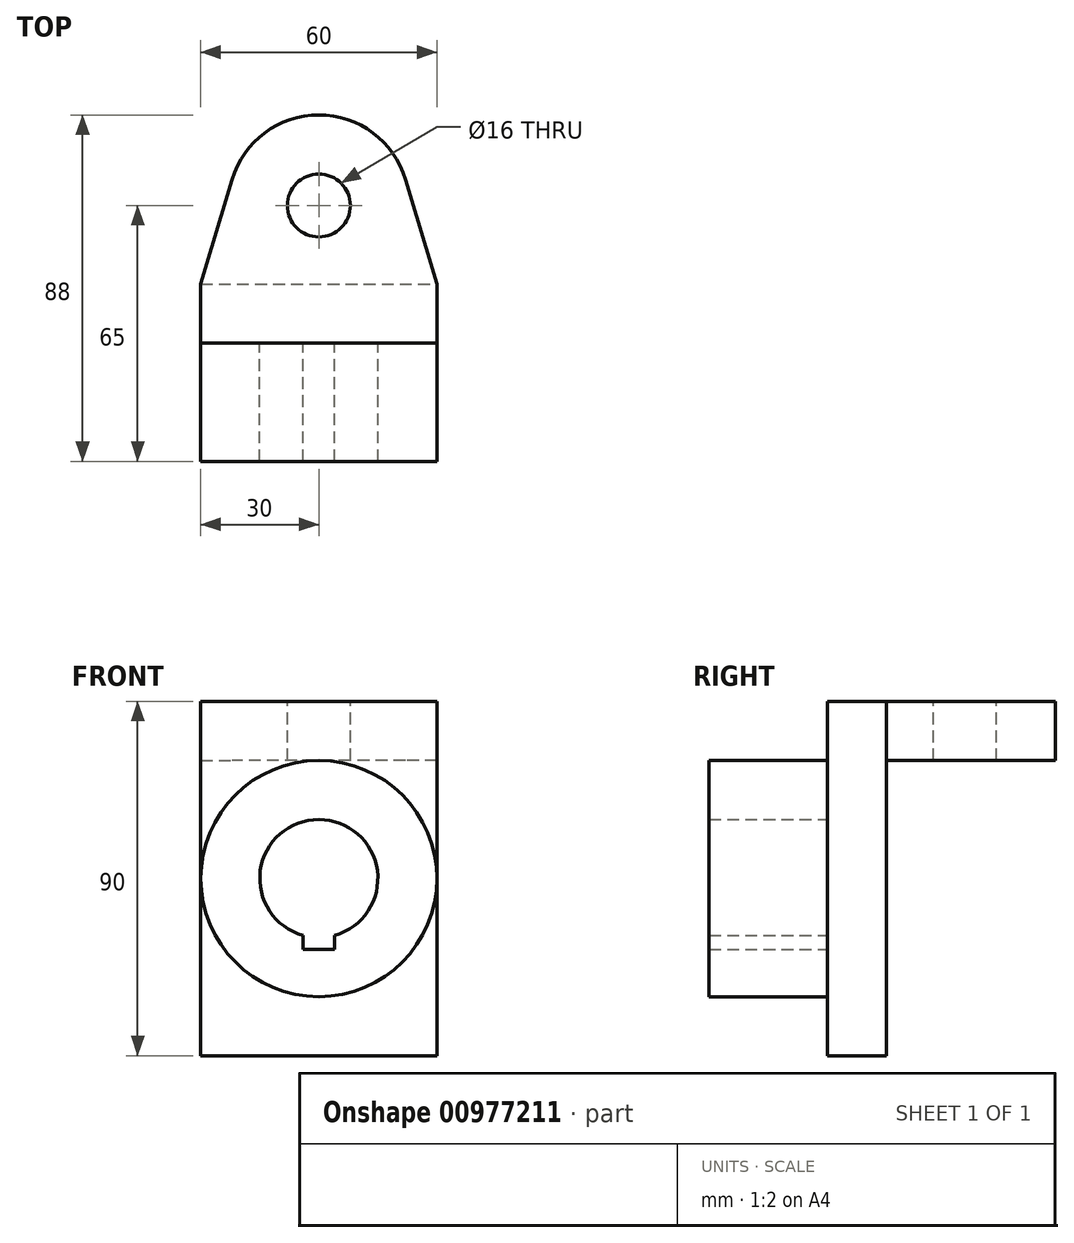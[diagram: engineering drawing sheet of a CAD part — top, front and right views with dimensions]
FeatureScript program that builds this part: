
annotation { "Feature Type Name" : "Feature", "Feature Type Description" : "" }
export const myFeature = defineFeature(function(context is Context, id is Id, definition is map)
    precondition{}
    {
        {
            var Q0;
            Q0=qCreatedBy(makeId("Front.planeOp"),FACE);
            var sketch = newSketch(context, id + "F0", { "sketchPlane" : qUnion([Q0])});
            skLineSegment(sketch, "E0.bottom", {"start": v(-30, 45) * mm, "end": v(30, 45) * mm});
            skLineSegment(sketch, "E0.top", {"start": v(-30, -45) * mm, "end": v(30, -45) * mm});
            skLineSegment(sketch, "E0.left", {"start": v(-30, 45) * mm, "end": v(-30, -45) * mm});
            skLineSegment(sketch, "E0.right", {"start": v(30, 45) * mm, "end": v(30, -45) * mm});
            skPoint(sketch, "E0.middle", {"position": v(0, 0) * mm});
            skSolve(sketch);
        }
        {
            var Q0;
            Q0 = qSketchRegion(id + "F0", true);
            extrude(context, id + "F1", {"entities" : qUnion([Q0]), "depth" : 15 * mm, "offsetDistance" : 25 * mm});
        }
        {
            var Q0;
            Q0=makeQuery(id+"F1.opExtrude","CAP_FACE",FACE,{"disambiguationData":[OSD([sQuery(id+"F0.wireOp",EDGE,"E0.bottom"),sQuery(id+"F0.wireOp",EDGE,"E0.top"),sQuery(id+"F0.wireOp",EDGE,"E0.left"),sQuery(id+"F0.wireOp",EDGE,"E0.right")])],"isStart":false});
            var sketch = newSketch(context, id + "F2", { "sketchPlane" : qUnion([Q0])});
            skCircle(sketch, "E1", {"center": v(0, 0) * mm, "radius": 30 * mm});
            skArc(sketch, "E2", {"start": v(4, -14.46) * mm, "mid": v(0, 15) * mm, "end": v(-4, -14.46) * mm});
            skLineSegment(sketch, "E3.top", {"start": v(0, -18) * mm, "end": v(4, -18) * mm});
            skLineSegment(sketch, "E3.right", {"start": v(4, -14.46) * mm, "end": v(4, -18) * mm});
            skLineSegment(sketch, "E4.MirrorCS", {"start": v(0, -18) * mm, "end": v(-4, -18) * mm});
            skLineSegment(sketch, "E5.MirrorCS", {"start": v(-4, -14.46) * mm, "end": v(-4, -18) * mm});
            skPoint(sketch, "E3.left.start.orphan", {"position": v(0, -15) * mm});
            skSolve(sketch);
        }
        {
            var Q0;
            Q0 = qSketchRegion(id + "F2", true);
            extrude(context, id + "F3", {"entities" : qUnion([Q0]), "operationType" : NewBodyOperationType.ADD, "depth" : 30 * mm, "offsetDistance" : 25 * mm});
        }
        {
            var Q0;
            Q0=makeQuery(id+"F1.opExtrude","SWEPT_FACE",FACE,{"disambiguationData":[OSD([sQuery(id+"F0.wireOp",EDGE,"E0.bottom")])]});
            var sketch = newSketch(context, id + "F4", { "sketchPlane" : qUnion([Q0])});
            skCircle(sketch, "E6", {"center": v(0, 20) * mm, "radius": 8 * mm});
            skArc(sketch, "E7", {"start": v(22.03, 26.6) * mm, "mid": v(0, 43) * mm, "end": v(-22.03, 26.6) * mm});
            skLineSegment(sketch, "E8", {"start": v(-30, 0) * mm, "end": v(30, 0) * mm});
            skLineSegment(sketch, "E9", {"start": v(30, 0) * mm, "end": v(22.03, 26.6) * mm});
            skLineSegment(sketch, "E10", {"start": v(-30, 0) * mm, "end": v(-22.03, 26.6) * mm});
            skPoint(sketch, "E11.orphan", {"position": v(17.61, 41.36) * mm});
            skPoint(sketch, "E12.orphan", {"position": v(-17.61, 41.36) * mm});
            skSolve(sketch);
        }
        {
            var Q0;
            Q0 = qSketchRegion(id + "F4", true);
            extrude(context, id + "F5", {"entities" : qUnion([Q0]), "operationType" : NewBodyOperationType.ADD, "oppositeDirection" : true, "depth" : 15 * mm, "offsetDistance" : 25 * mm});
        }
    });
